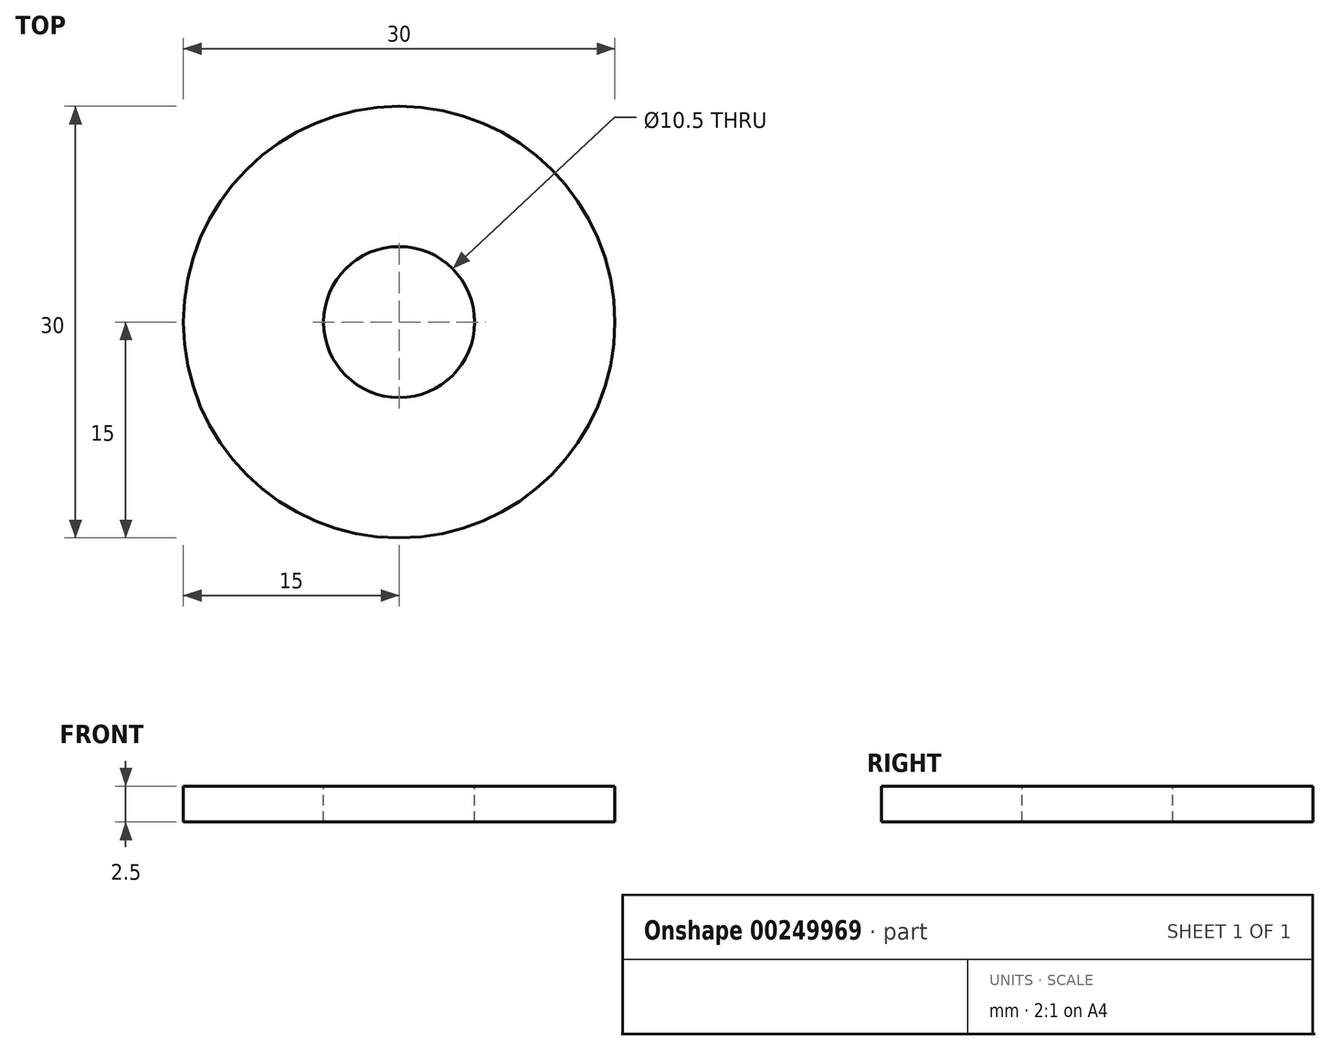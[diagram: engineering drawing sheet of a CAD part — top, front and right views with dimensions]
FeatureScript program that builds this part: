
annotation { "Feature Type Name" : "Feature", "Feature Type Description" : "" }
export const myFeature = defineFeature(function(context is Context, id is Id, definition is map)
    precondition{}
    {
        {
            var Q0;
            Q0=qCreatedBy(makeId("Front.planeOp"),FACE);
            var sketch = newSketch(context, id + "F0", { "sketchPlane" : qUnion([Q0])});
            skLineSegment(sketch, "E0", {"start": v(-15, 2.5) * mm, "end": v(-5.25, 2.5) * mm});
            skLineSegment(sketch, "E1", {"start": v(-5.25, 0) * mm, "end": v(-5.25, 2.5) * mm});
            skLineSegment(sketch, "E2", {"start": v(-15, 0) * mm, "end": v(-15, 2.5) * mm});
            skLineSegment(sketch, "E3", {"start": v(-15, 0) * mm, "end": v(-5.25, 0) * mm});
            skPoint(sketch, "E4.orphan", {"position": v(0, 2.5) * mm});
            skLineSegment(sketch, "E5", {"start": v(0, 25.32) * mm, "end": v(0, -10.45) * mm, "construction": true});
            skSolve(sketch);
        }
        {
            var Q0;
            Q0 = qSketchRegion(id + "F0", true);
            var Q1;
            Q1=sQuery(id+"F0.wireOp",EDGE,"E5");
            revolve(context, id + "F1", {"entities" : qUnion([Q0]), "axis" : qUnion([Q1]), "revolveType" : RevolveType.FULL});
        }
    });
